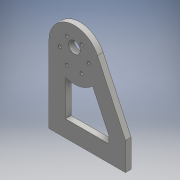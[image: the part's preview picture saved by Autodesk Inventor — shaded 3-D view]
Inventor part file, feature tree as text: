
AUTODESK INVENTOR PART (.ipt)
format: ipt  version: 2016 (Build 200138000, 138)  size: 125,952 bytes
history: native  units: mm
features: extrude x1, sketch x1
ambient origin geometry x8: Origin, YZ Plane, XZ Plane, XY Plane, X Axis, Y Axis, Z Axis, Center Point
bodies: Solid1 (feature_tree)
feature tree (2):
  extrude  "Extrusion1"  Depth=18.0mm
  sketch  "Sketch1"  dims[d7=18.0mm d9=18.0mm d10=18.0mm d11=18.0mm d12=18.0mm d13=82.5mm d14=12.5mm d15=7.0mm d16=3.2mm d17=15.5mm d18=60.0mm d20=360.0deg d22=30.0mm d23=27.5mm d24=18.0mm d25=27.5mm d26=27.5mm d27=27.5mm d29=18.0mm d30=18.0mm d31=82.5mm d32=82.5mm d33=6.0mm d34=0.0mm]
